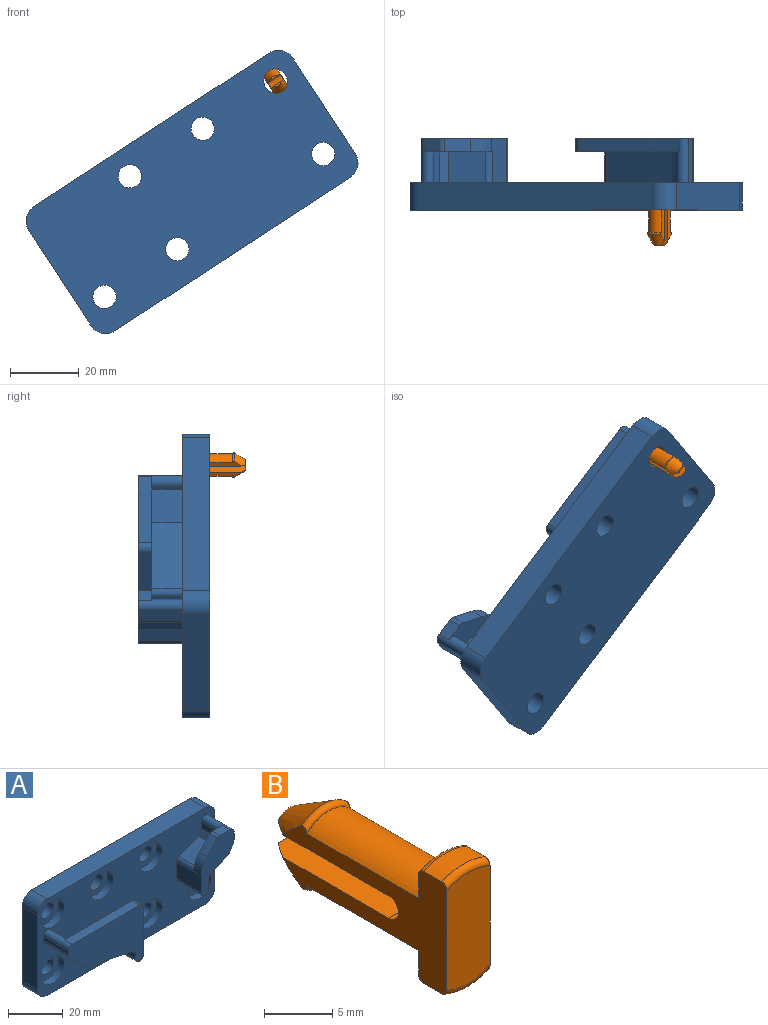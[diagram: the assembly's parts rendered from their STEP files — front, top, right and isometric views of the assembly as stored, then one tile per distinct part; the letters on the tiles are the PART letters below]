
ASSEMBLY  parts=2 mates=1
PART A: 66 faces, bbox 92x21x43.3 mm
  f0: plane 23.83x13mm, normal (-0.21,0,-0.98), area 316.9mm2, adj f5,f11,f16,f43
  f1: plane 21x13mm, normal (1,0,0), area 132.4mm2, adj f5,f9,f12,f14,f17,f43
  f2: plane 35x4mm, normal (0,0,1), area 140mm2, adj f5,f9,f13,f17
  f3: plane 13x1.83mm, normal (-1,0,0), area 23.8mm2, adj f5,f13,f15,f43
  f4: plane 13x8mm, normal (-0.71,0,-0.71), area 147.1mm2, adj f5,f15,f16,f43
  f5: plane 39x25mm, normal (0,-1,0), area 607mm2, adj f0,f1,f2,f3,f4,f10,f11,f12
  f6: plane 26.42x9mm, normal (0.21,0,0.98), area 243.2mm2, adj f8,f9,f14,f43
  f7: plane 9x1mm, normal (1,0,0), area 9mm2, adj f8,f9,f13,f43
  f8: plane 9x7mm, normal (0.71,0,0.71), area 89.1mm2, adj f6,f7,f9,f43
  f9: plane 37x17.62mm, normal (0,1,0), area 410mm2, adj f1,f2,f6,f7,f8,f13,f14,f17
  f10: plane 13x2.15mm, normal (-1,0,0), area 27.9mm2, adj f5,f11,f12,f43
  f11: cylinder r=2mm len=13mm, axis (0,-1,0), area 35.4mm2, adj f0,f5,f10,f43
  f12: cylinder r=2mm len=13mm, axis (0,-1,0), area 81.7mm2, adj f1,f5,f10,f43
  f13: cylinder r=2mm len=13mm, axis (0,1,0), area 69.1mm2, adj f2,f3,f5,f7,f9,f43
  f14: cylinder r=2mm len=9mm, axis (0,-1,0), area 24.5mm2, adj f1,f6,f9,f43
  f15: cylinder r=2mm len=13mm, axis (0,1,0), area 20.4mm2, adj f3,f4,f5,f43
  f16: cylinder r=2mm len=13mm, axis (0,1,0), area 14.9mm2, adj f0,f4,f5,f43
  f17: cylinder r=2mm len=4mm, axis (0,1,0), area 12.6mm2, adj f1,f2,f5,f9
  f18: plane 13x8.31mm, normal (0.36,0,-0.93), area 115.6mm2, adj f24,f30,f34,f43
  f19: plane 13x3.68mm, normal (0.87,0,-0.5), area 55.2mm2, adj f24,f34,f35,f43
  f20: plane 13x3.54mm, normal (1,0,0), area 46mm2, adj f24,f32,f35,f43
  f21: plane 5.17x4mm, normal (0,0,1), area 20.7mm2, adj f24,f28,f32,f36
  f22: plane 5.49x5.49mm, normal (-0.71,0,0.71), area 31mm2, adj f24,f28,f36,f37
  f23: plane 13x7.86mm, normal (-1,0,0), area 100mm2, adj f24,f28,f31,f33,f37,f43
  f24: plane 23x17mm, normal (0,-1,0), area 201.3mm2, adj f18,f19,f20,f21,f22,f23,f29,f30
  f25: plane 10.22x9mm, normal (-0.36,0,0.93), area 98.4mm2, adj f26,f28,f33,f43
  f26: plane 9x2.6mm, normal (-0.87,0,0.5), area 27mm2, adj f25,f27,f28,f43
  f27: plane 9x3mm, normal (-1,0,0), area 27mm2, adj f26,f28,f32,f43
  f28: plane 15x13.38mm, normal (0,1,0), area 80.6mm2, adj f21,f22,f23,f25,f26,f27,f32,f33
  f29: plane 13x4.87mm, normal (1,0,0), area 63.3mm2, adj f24,f30,f31,f43
  f30: cylinder r=2mm len=13mm, axis (0,1,0), area 31.3mm2, adj f18,f24,f29,f43
  f31: cylinder r=2mm len=13mm, axis (0,1,0), area 81.7mm2, adj f23,f24,f29,f43
  f32: cylinder r=2mm len=13mm, axis (0,1,0), area 69.1mm2, adj f20,f21,f24,f27,f28,f43
  f33: cylinder r=2mm len=9mm, axis (0,-1,0), area 21.7mm2, adj f23,f25,f28,f43
  f34: cylinder r=2mm len=13mm, axis (0,1,0), area 17.7mm2, adj f18,f19,f24,f43
  f35: cylinder r=2mm len=13mm, axis (0,1,0), area 13.6mm2, adj f19,f20,f24,f43
  f36: cylinder r=2mm len=4mm, axis (0,1,0), area 6.3mm2, adj f21,f22,f24,f28
  f37: cylinder r=10mm len=7.07mm, axis (0,1,0), area 31.4mm2, adj f22,f23,f24,f28
  f38: plane 82x8mm, normal (0,0,1), area 656mm2, adj f42,f43,f44,f47
  f39: plane 33.3x8mm, normal (-1,0,0), area 266.4mm2, adj f42,f43,f44,f45
  f40: plane 82x8mm, normal (0,0,-1), area 656mm2, adj f42,f43,f45,f46
  f41: plane 33.3x8mm, normal (1,0,0), area 266.4mm2, adj f42,f43,f46,f47
  f42: plane 92x43.3mm, normal (0,1,0), area 3744.2mm2, adj f38,f39,f40,f41,f44,f45,f46,f47
  f43: plane 92x43.3mm, normal (0,-1,0), area 2965.9mm2, adj f0,f1,f3,f4,f6,f7,f8,f10
  f44: cylinder r=5mm len=8mm, axis (0,1,0), area 62.8mm2, adj f38,f39,f42,f43
  f45: cylinder r=5mm len=8mm, axis (0,-1,0), area 62.8mm2, adj f39,f40,f42,f43
  f46: cylinder r=5mm len=8mm, axis (0,1,0), area 62.8mm2, adj f40,f41,f42,f43
  f47: cylinder r=5mm len=8mm, axis (0,-1,0), area 62.8mm2, adj f38,f41,f42,f43
  f48: cylinder r=3.4mm len=6.8mm, axis (0,-1,0), area 106.8mm2, adj f42,f49
  f49: plane 12x12mm, normal (0,-1,0), area 76.8mm2, adj f48,f50
  f50: cylinder r=6mm len=12mm, axis (0,-1,0), area 113.1mm2, adj f43,f49
  f51: cylinder r=3.4mm len=6.8mm, axis (0,-1,0), area 106.8mm2, adj f42,f52
  f52: plane 12x12mm, normal (0,-1,0), area 76.8mm2, adj f51,f53
  f53: cylinder r=6mm len=12mm, axis (0,-1,0), area 113.1mm2, adj f43,f52
  f54: cylinder r=3.4mm len=6.8mm, axis (0,-1,0), area 106.8mm2, adj f42,f55
  f55: plane 12x12mm, normal (0,-1,0), area 76.8mm2, adj f54,f56
  f56: cylinder r=6mm len=12mm, axis (0,-1,0), area 113.1mm2, adj f43,f55
  f57: cylinder r=3.4mm len=6.8mm, axis (0,-1,0), area 106.8mm2, adj f42,f58
  f58: plane 12x12mm, normal (0,-1,0), area 76.8mm2, adj f57,f59
  f59: cylinder r=6mm len=12mm, axis (0,-1,0), area 113.1mm2, adj f43,f58
  f60: cylinder r=3.4mm len=6.8mm, axis (0,-1,0), area 106.8mm2, adj f42,f61
  f61: plane 12x12mm, normal (0,-1,0), area 76.8mm2, adj f60,f62
  f62: cylinder r=6mm len=12mm, axis (0,-1,0), area 113.1mm2, adj f43,f61
  f63: cylinder r=3.4mm len=6.8mm, axis (0,-1,0), area 106.8mm2, adj f42,f64
  f64: plane 12x12mm, normal (0,-1,0), area 76.8mm2, adj f63,f65
  f65: cylinder r=6mm len=12mm, axis (0,-1,0), area 113.1mm2, adj f43,f64
PART B: 24 faces, bbox 6.6x18.6x12 mm
  f0: cone r=3.55mm half-angle=30deg, axis (0,-1,0), area 18.5mm2, adj f1,f15,f16,f18,f19
  f1: torus R=3.2mm, axis (0,-1,0), area 4.1mm2, adj f0,f2,f18,f19
  f2: plane 4.5x0.97mm, normal (0,1,0), area 0.2mm2, adj f1,f7,f18,f19
  f3: cone r=3.55mm half-angle=30deg, axis (0,-1,0), area 18.5mm2, adj f4,f13,f17,f18,f19
  f4: torus R=3.2mm, axis (0,-1,0), area 4.1mm2, adj f3,f5,f18,f19
  f5: plane 4.5x0.97mm, normal (0,1,0), area 0.2mm2, adj f4,f6,f18,f19
  f6: cylinder r=3.25mm len=11.6mm, axis (0,-1,0), area 57.7mm2, adj f5,f8,f18,f19
  f7: cylinder r=3.25mm len=11.6mm, axis (0,-1,0), area 57.7mm2, adj f2,f9,f18,f19
  f8: plane 4.5x2.65mm, normal (0,1,0), area 8.4mm2, adj f6,f18,f19,f22
  f9: plane 4.5x2.65mm, normal (0,1,0), area 8.4mm2, adj f7,f18,f19,f20
  f10: cylinder r=5.5mm len=4.5mm, axis (0,-1,0), area 8.8mm2, adj f18,f19,f22,f23
  f11: cylinder r=5.5mm len=4.5mm, axis (0,-1,0), area 8.8mm2, adj f18,f19,f20,f21
  f12: plane 10x4.5mm, normal (0,-1,0), area 43.4mm2, adj f18,f19,f21,f23
  f13: plane 12.63x4.63mm, normal (0,0,-1), area 54.7mm2, adj f3,f14,f17,f18,f19
  f14: cylinder r=1mm len=4.5mm, axis (1,0,0), area 14.1mm2, adj f13,f15,f18,f19
  f15: plane 12.63x4.63mm, normal (0,0,1), area 54.7mm2, adj f0,f14,f16,f18,f19
  f16: plane 2.46x0.58mm, normal (0,1,0), area 1mm2, adj f0,f15
  f17: plane 2.46x0.58mm, normal (0,1,0), area 1mm2, adj f3,f13
  f18: plane 17.09x10.14mm, normal (-1,0,0), area 70.4mm2, adj f0,f1,f2,f3,f4,f5,f6,f7
  f19: plane 17.09x10.14mm, normal (1,0,0), area 70.4mm2, adj f0,f1,f2,f3,f4,f5,f6,f7
  f20: torus R=5mm, axis (0,1,0), area 3.7mm2, adj f9,f11,f18,f19
  f21: torus R=5mm, axis (0,-1,0), area 3.7mm2, adj f11,f12,f18,f19
  f22: torus R=5mm, axis (0,1,0), area 3.7mm2, adj f8,f10,f18,f19
  f23: torus R=5mm, axis (0,-1,0), area 3.7mm2, adj f10,f12,f18,f19
PLACE A rot(axis=(0.29,0,-0.96),180deg) t=(-57.42,11.71,-16.29)mm
PLACE B rot(axis=(0.29,0,-0.96),180deg) t=(-32.97,3.71,8.64)mm
MATE revolute B.f0 <-> A.f48  axis (0,-1,0) through (-32.97,3.71,8.64)mm
